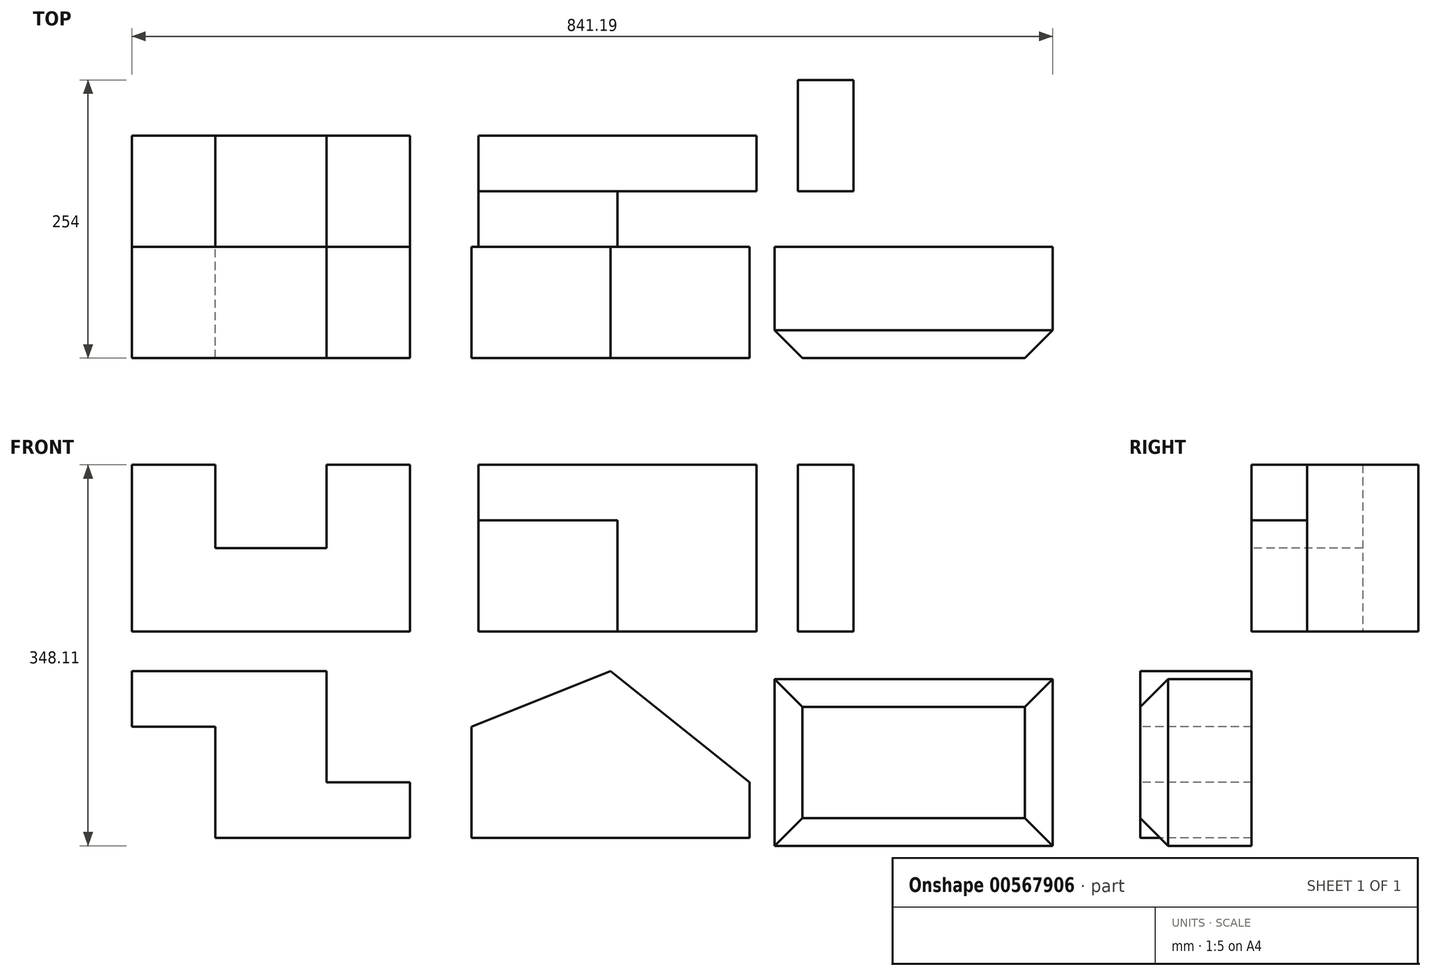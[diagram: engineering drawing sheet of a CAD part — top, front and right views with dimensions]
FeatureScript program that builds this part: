
annotation { "Feature Type Name" : "Feature", "Feature Type Description" : "" }
export const myFeature = defineFeature(function(context is Context, id is Id, definition is map)
    precondition{}
    {
        {
            var Q0;
            Q0=qCreatedBy(makeId("Front.planeOp"),FACE);
            var sketch = newSketch(context, id + "F0", { "sketchPlane" : qUnion([Q0])});
            skLineSegment(sketch, "E0", {"start": v(0, 0) * mm, "end": v(254, 0) * mm});
            skLineSegment(sketch, "E1", {"start": v(0, 0) * mm, "end": v(0, 152.4) * mm});
            skLineSegment(sketch, "E2", {"start": v(76.2, 152.4) * mm, "end": v(76.2, 76.2) * mm});
            skLineSegment(sketch, "E3", {"start": v(0, 152.4) * mm, "end": v(76.2, 152.4) * mm});
            skLineSegment(sketch, "E4", {"start": v(254, 0) * mm, "end": v(254, 152.4) * mm});
            skLineSegment(sketch, "E5", {"start": v(254, 152.4) * mm, "end": v(177.8, 152.4) * mm});
            skLineSegment(sketch, "E6", {"start": v(177.8, 152.4) * mm, "end": v(177.8, 76.2) * mm});
            skLineSegment(sketch, "E7", {"start": v(177.8, 76.2) * mm, "end": v(76.2, 76.2) * mm});
            skSolve(sketch);
        }
        {
            var Q0;
            Q0=makeQuery(id+"F0.imprint","IMPRINT",FACE,{"disambiguationData":[TD([[makeQuery(id+"F0.imprint","IMPRINT",EDGE,{"derivedFrom":sQuery(id+"F0.wireOp",EDGE,"E0")}),1.0]])]});
            extrude(context, id + "F1", {"entities" : qUnion([Q0]), "oppositeDirection" : true, "depth" : 101.6 * mm, "offsetDistance" : 25.4 * mm});
        }
        {
            var Q0;
            Q0=qCreatedBy(makeId("Top.planeOp"),FACE);
            var sketch = newSketch(context, id + "F2", { "sketchPlane" : qUnion([Q0])});
            skLineSegment(sketch, "E8", {"start": v(316.47, 0) * mm, "end": v(316.47, 101.6) * mm});
            skLineSegment(sketch, "E9", {"start": v(316.47, 101.6) * mm, "end": v(570.47, 101.6) * mm});
            skLineSegment(sketch, "E10", {"start": v(570.47, 101.6) * mm, "end": v(570.47, 50.8) * mm});
            skLineSegment(sketch, "E11", {"start": v(570.47, 50.8) * mm, "end": v(443.47, 50.8) * mm});
            skLineSegment(sketch, "E12", {"start": v(443.47, 50.8) * mm, "end": v(443.47, 0) * mm});
            skLineSegment(sketch, "E13", {"start": v(443.47, 0) * mm, "end": v(316.47, 0) * mm});
            skSolve(sketch);
        }
        {
            var Q0;
            Q0=makeQuery(id+"F2.imprint","IMPRINT",FACE,{"disambiguationData":[TD([[makeQuery(id+"F2.imprint","IMPRINT",EDGE,{"derivedFrom":sQuery(id+"F2.wireOp",EDGE,"E8")}),-1.0]])]});
            extrude(context, id + "F3", {"entities" : qUnion([Q0]), "depth" : 152.4 * mm, "offsetDistance" : 25.4 * mm});
        }
        {
            var Q0;
            Q0=makeQuery(id+"F3.opExtrude","SWEPT_FACE",FACE,{"disambiguationData":[OSD([sQuery(id+"F2.wireOp",EDGE,"E13")])]});
            var sketch = newSketch(context, id + "F4", { "sketchPlane" : qUnion([Q0])});
            skLineSegment(sketch, "E14.bottom", {"start": v(316.47, 152.4) * mm, "end": v(443.47, 152.4) * mm});
            skLineSegment(sketch, "E14.top", {"start": v(316.47, 101.6) * mm, "end": v(443.47, 101.6) * mm});
            skLineSegment(sketch, "E14.left", {"start": v(316.47, 152.4) * mm, "end": v(316.47, 101.6) * mm});
            skLineSegment(sketch, "E14.right", {"start": v(443.47, 152.4) * mm, "end": v(443.47, 101.6) * mm});
            skSolve(sketch);
        }
        {
            var Q0;
            Q0=makeQuery(id+"F4.imprint","IMPRINT",FACE,{"disambiguationData":[TD([[makeQuery(id+"F4.imprint","IMPRINT",EDGE,{"derivedFrom":sQuery(id+"F4.wireOp",EDGE,"E14.bottom")}),1.0]])]});
            extrude(context, id + "F5", {"entities" : qUnion([Q0]), "operationType" : NewBodyOperationType.REMOVE, "oppositeDirection" : true, "depth" : 50.8 * mm, "offsetDistance" : 25.4 * mm});
        }
        {
            var Q0;
            Q0=makeQuery(id+"F5.boolean.opBoolean","MERGE",FACE,{"derivedFrom":[makeQuery(id+"F3.opExtrude","SWEPT_FACE",FACE,{"disambiguationData":[OSD([sQuery(id+"F2.wireOp",EDGE,"E11")])]}),makeQuery(id+"F5.opExtrude","CAP_FACE",FACE,{"disambiguationData":[OSD([sQuery(id+"F4.wireOp",EDGE,"E14.bottom"),sQuery(id+"F4.wireOp",EDGE,"E14.top"),sQuery(id+"F4.wireOp",EDGE,"E14.left"),sQuery(id+"F4.wireOp",EDGE,"E14.right")])],"isStart":false})]});
            var sketch = newSketch(context, id + "F6", { "sketchPlane" : qUnion([Q0])});
            skLineSegment(sketch, "E15", {"start": v(608.54, 0) * mm, "end": v(608.54, 152.4) * mm});
            skLineSegment(sketch, "E16", {"start": v(608.54, 152.4) * mm, "end": v(786.34, 152.4) * mm});
            skLineSegment(sketch, "E17", {"start": v(786.34, 152.4) * mm, "end": v(786.34, 50.8) * mm});
            skLineSegment(sketch, "E18", {"start": v(786.34, 50.8) * mm, "end": v(862.54, 50.8) * mm});
            skLineSegment(sketch, "E19", {"start": v(862.54, 50.8) * mm, "end": v(862.54, 0) * mm});
            skLineSegment(sketch, "E20", {"start": v(862.54, 0) * mm, "end": v(608.54, 0) * mm});
            skLineSegment(sketch, "E21", {"start": v(659.34, 152.4) * mm, "end": v(659.34, 0) * mm});
            skLineSegment(sketch, "E22", {"start": v(608.54, 152.4) * mm, "end": v(659.34, 152.4) * mm});
            skSolve(sketch);
        }
        {
            var Q0;
            {var subQ0=sQuery(id+"F6.wireOp",EDGE,"E15");Q0=makeQuery(id+"F6.imprint","IMPRINT",FACE,{"disambiguationData":[TD([[makeQuery(id+"F6.imprint","IMPRINT",EDGE,{"derivedFrom":subQ0}),-1.0]])]});}
            var Q1;
            Q1=makeQuery(id+"F6.imprint","IMPRINT",FACE,{"disambiguationData":[TD([[makeQuery(id+"F6.imprint","IMPRINT",EDGE,{"derivedFrom":sQuery(id+"F6.wireOp",EDGE,"E16")}),-1.0]])]});
            extrude(context, id + "F7", {"entities" : qUnion([Q0, Q1]), "oppositeDirection" : true, "depth" : 101.6 * mm, "offsetDistance" : 25.4 * mm});
        }
        {
            var Q0;
            Q0=makeQuery(id+"F7.opExtrude","SWEPT_FACE",FACE,{"disambiguationData":[OSD([sQuery(id+"F6.wireOp",EDGE,"E16"),sQuery(id+"F6.wireOp",EDGE,"E22")])]});
            var sketch = newSketch(context, id + "F8", { "sketchPlane" : qUnion([Q0])});
            skLineSegment(sketch, "E23.bottom", {"start": v(659.34, 50.8) * mm, "end": v(735.54, 50.8) * mm});
            skLineSegment(sketch, "E23.top", {"start": v(659.34, 101.6) * mm, "end": v(735.54, 101.6) * mm});
            skLineSegment(sketch, "E23.left", {"start": v(659.34, 50.8) * mm, "end": v(659.34, 101.6) * mm});
            skLineSegment(sketch, "E23.right", {"start": v(735.54, 50.8) * mm, "end": v(735.54, 101.6) * mm});
            skLineSegment(sketch, "E24", {"start": v(659.34, 50.8) * mm, "end": v(608.54, 50.8) * mm});
            skSolve(sketch);
        }
        {
            var Q0;
            Q0=makeQuery(id+"F8.imprint","IMPRINT",FACE,{"disambiguationData":[TD([[makeQuery(id+"F8.imprint","IMPRINT",EDGE,{"derivedFrom":sQuery(id+"F8.wireOp",EDGE,"E23.bottom")}),1.0]])]});
            extrude(context, id + "F9", {"entities" : qUnion([Q0]), "operationType" : NewBodyOperationType.REMOVE, "oppositeDirection" : true, "depth" : 152.4 * mm, "offsetDistance" : 25.4 * mm});
        }
        {
            var Q0;
            Q0=qCreatedBy(makeId("Front.planeOp"),FACE);
            var sketch = newSketch(context, id + "F10", { "sketchPlane" : qUnion([Q0])});
            skLineSegment(sketch, "E25", {"start": v(0, -36.2) * mm, "end": v(177.8, -36.2) * mm});
            skLineSegment(sketch, "E26", {"start": v(177.8, -36.2) * mm, "end": v(177.8, -137.8) * mm});
            skLineSegment(sketch, "E27", {"start": v(177.8, -137.8) * mm, "end": v(254, -137.8) * mm});
            skLineSegment(sketch, "E28", {"start": v(254, -137.8) * mm, "end": v(254, -188.6) * mm});
            skLineSegment(sketch, "E29", {"start": v(254, -188.6) * mm, "end": v(76.2, -188.6) * mm});
            skLineSegment(sketch, "E30", {"start": v(76.2, -188.6) * mm, "end": v(76.2, -87) * mm});
            skLineSegment(sketch, "E31", {"start": v(76.2, -87) * mm, "end": v(0, -87) * mm});
            skLineSegment(sketch, "E32", {"start": v(0, -36.2) * mm, "end": v(0, -87) * mm});
            skSolve(sketch);
        }
        {
            var Q0;
            Q0=makeQuery(id+"F10.imprint","IMPRINT",FACE,{"disambiguationData":[TD([[makeQuery(id+"F10.imprint","IMPRINT",EDGE,{"derivedFrom":sQuery(id+"F10.wireOp",EDGE,"E25")}),-1.0]])]});
            extrude(context, id + "F11", {"entities" : qUnion([Q0]), "depth" : 101.6 * mm, "offsetDistance" : 25.4 * mm});
        }
        {
            var Q0;
            Q0=makeQuery(id+"F11.opExtrude","CAP_FACE",FACE,{"disambiguationData":[OSD([sQuery(id+"F10.wireOp",EDGE,"E25"),sQuery(id+"F10.wireOp",EDGE,"E26"),sQuery(id+"F10.wireOp",EDGE,"E27"),sQuery(id+"F10.wireOp",EDGE,"E28"),sQuery(id+"F10.wireOp",EDGE,"E29"),sQuery(id+"F10.wireOp",EDGE,"E30"),sQuery(id+"F10.wireOp",EDGE,"E31"),sQuery(id+"F10.wireOp",EDGE,"E32")])],"isStart":false});
            var sketch = newSketch(context, id + "F12", { "sketchPlane" : qUnion([Q0])});
            skLineSegment(sketch, "E33", {"start": v(310.15, -188.6) * mm, "end": v(310.15, -87) * mm});
            skLineSegment(sketch, "E34", {"start": v(310.15, -87) * mm, "end": v(437.15, -36.2) * mm});
            skLineSegment(sketch, "E35", {"start": v(310.15, -188.6) * mm, "end": v(564.15, -188.6) * mm});
            skLineSegment(sketch, "E36", {"start": v(564.15, -188.6) * mm, "end": v(564.15, -137.8) * mm});
            skLineSegment(sketch, "E37", {"start": v(437.15, -36.2) * mm, "end": v(564.15, -137.8) * mm});
            skSolve(sketch);
        }
        {
            var Q0;
            Q0=makeQuery(id+"F12.imprint","IMPRINT",FACE,{"disambiguationData":[TD([[makeQuery(id+"F12.imprint","IMPRINT",EDGE,{"derivedFrom":sQuery(id+"F12.wireOp",EDGE,"E33")}),-1.0]])]});
            extrude(context, id + "F13", {"entities" : qUnion([Q0]), "oppositeDirection" : true, "depth" : 101.6 * mm, "offsetDistance" : 25.4 * mm});
        }
        {
            var Q0;
            Q0=makeQuery(id+"F13.opExtrude","CAP_FACE",FACE,{"disambiguationData":[OSD([sQuery(id+"F12.wireOp",EDGE,"E33"),sQuery(id+"F12.wireOp",EDGE,"E34"),sQuery(id+"F12.wireOp",EDGE,"E35"),sQuery(id+"F12.wireOp",EDGE,"E36"),sQuery(id+"F12.wireOp",EDGE,"E37")])],"isStart":true});
            var sketch = newSketch(context, id + "F14", { "sketchPlane" : qUnion([Q0])});
            skLineSegment(sketch, "E38", {"start": v(587.19, -43.3) * mm, "end": v(841.19, -43.3) * mm});
            skLineSegment(sketch, "E39", {"start": v(841.19, -43.3) * mm, "end": v(841.19, -195.7) * mm});
            skLineSegment(sketch, "E40", {"start": v(841.19, -195.7) * mm, "end": v(587.19, -195.7) * mm});
            skLineSegment(sketch, "E41", {"start": v(587.19, -43.3) * mm, "end": v(587.19, -195.7) * mm});
            skSolve(sketch);
        }
        {
            var Q0;
            Q0 = qSketchRegion(id + "F14", true);
            extrude(context, id + "F15", {"entities" : qUnion([Q0]), "oppositeDirection" : true, "depth" : 101.6 * mm, "offsetDistance" : 25.4 * mm});
        }
        {
            var Q0;
            Q0=makeQuery(id+"F15.opExtrude","CAP_EDGE",EDGE,{"disambiguationData":[OSD([sQuery(id+"F14.wireOp",EDGE,"E38")])],"isStart":true});
            var Q1;
            Q1=makeQuery(id+"F15.opExtrude","CAP_EDGE",EDGE,{"disambiguationData":[OSD([sQuery(id+"F14.wireOp",EDGE,"E40")])],"isStart":true});
            var Q2;
            Q2=makeQuery(id+"F15.opExtrude","CAP_EDGE",EDGE,{"disambiguationData":[OSD([sQuery(id+"F14.wireOp",EDGE,"E39")])],"isStart":true});
            var Q3;
            Q3=makeQuery(id+"F15.opExtrude","CAP_EDGE",EDGE,{"disambiguationData":[OSD([sQuery(id+"F14.wireOp",EDGE,"E41")])],"isStart":true});
            chamfer(context, id + "F16", {"entities" : qUnion([Q0, Q1, Q2, Q3]), "width" : 25.4 * mm, "tangentPropagation" : true});
        }
    });
